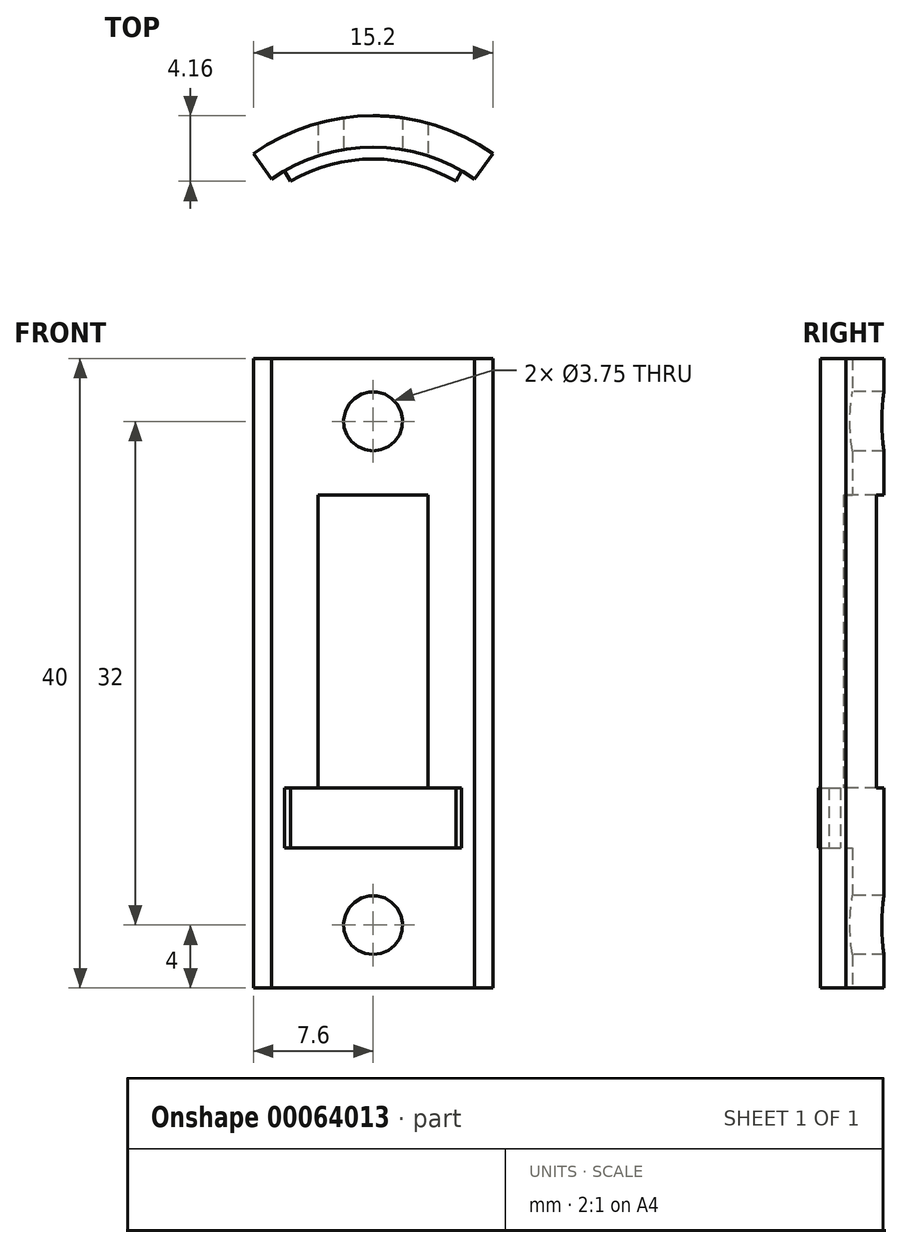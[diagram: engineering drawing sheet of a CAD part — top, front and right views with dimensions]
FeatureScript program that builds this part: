
annotation { "Feature Type Name" : "Feature", "Feature Type Description" : "" }
export const myFeature = defineFeature(function(context is Context, id is Id, definition is map)
    precondition{}
    {
        {
            var Q0;
            Q0=qCreatedBy(makeId("Top.planeOp"),FACE);
            var sketch = newSketch(context, id + "F0", { "sketchPlane" : qUnion([Q0])});
            skArc(sketch, "E0", {"start": v(6.45, 9.22) * mm, "mid": v(0, 11.25) * mm, "end": v(-6.45, 9.22) * mm});
            skArc(sketch, "E1", {"start": v(7.6, 10.85) * mm, "mid": v(0, 13.25) * mm, "end": v(-7.6, 10.85) * mm});
            skLineSegment(sketch, "E2", {"start": v(6.45, 9.22) * mm, "end": v(7.6, 10.85) * mm});
            skLineSegment(sketch, "E3", {"start": v(-6.45, 9.22) * mm, "end": v(-7.6, 10.85) * mm});
            skSolve(sketch);
        }
        {
            var Q0;
            Q0 = qSketchRegion(id + "F0", true);
            extrude(context, id + "F1", {"entities" : qUnion([Q0]), "depth" : 40 * mm});
        }
        {
            var Q0;
            Q0=qCreatedBy(makeId("Top.planeOp"),FACE);
            var sketch = newSketch(context, id + "F2", { "sketchPlane" : qUnion([Q0])});
            skArc(sketch, "E4", {"start": v(5.25, 9.1) * mm, "mid": v(0, 10.5) * mm, "end": v(-5.25, 9.1) * mm});
            skArc(sketch, "E5", {"start": v(5.62, 9.74) * mm, "mid": v(0, 11.25) * mm, "end": v(-5.62, 9.74) * mm});
            skLineSegment(sketch, "E6", {"start": v(-5.25, 9.1) * mm, "end": v(-5.62, 9.74) * mm});
            skLineSegment(sketch, "E7", {"start": v(5.25, 9.1) * mm, "end": v(5.62, 9.74) * mm});
            skSolve(sketch);
        }
        {
            var Q0;
            Q0 = qSketchRegion(id + "F2", true);
            extrude(context, id + "F3", {"entities" : qUnion([Q0]), "operationType" : NewBodyOperationType.ADD, "depth" : 12.7 * mm});
        }
        {
            var Q0;
            Q0 = qSketchRegion(id + "F2", true);
            extrude(context, id + "F4", {"entities" : qUnion([Q0]), "operationType" : NewBodyOperationType.REMOVE, "depth" : 8.9 * mm});
        }
        {
            var Q0;
            Q0=qCreatedBy(makeId("Front.planeOp"),FACE);
            var sketch = newSketch(context, id + "F5", { "sketchPlane" : qUnion([Q0])});
            skLineSegment(sketch, "E8", {"start": v(0, 36) * mm, "end": v(0, 4) * mm});
            skSolve(sketch);
        }
        {
            var Q0;
            Q0=sQuery(id+"F5.wireOp",VERTEX,"E8.start");
            var Q1;
            Q1=sQuery(id+"F5.wireOp",VERTEX,"E8.end");
            var Q2;
            Q2=makeQuery(id+"F1.opExtrude","SWEPT_BODY",BODY,{"disambiguationData":[OSD([sQuery(id+"F0.wireOp",EDGE,"E0"),sQuery(id+"F0.wireOp",EDGE,"E1"),sQuery(id+"F0.wireOp",EDGE,"E2"),sQuery(id+"F0.wireOp",EDGE,"E3")])]});
            hole(context, id + "F6", {"style" : HoleStyle.SIMPLE, "holeDiameter" : 3.75 * mm, "endStyle" : HoleEndStyle.THROUGH, "locations" : qUnion([Q0, Q1]), "scope" : qUnion([Q2])});
        }
        {
            var Q0;
            Q0=qCreatedBy(makeId("Front.planeOp"),FACE);
            var sketch = newSketch(context, id + "F7", { "sketchPlane" : qUnion([Q0])});
            skLineSegment(sketch, "E9.rect.bottom", {"start": v(-3.5, 12.7) * mm, "end": v(3.5, 12.7) * mm});
            skLineSegment(sketch, "E9.rect.top", {"start": v(3.5, 31.32) * mm, "end": v(-3.5, 31.32) * mm});
            skLineSegment(sketch, "E9.rect.left", {"start": v(-3.5, 12.7) * mm, "end": v(-3.5, 31.32) * mm});
            skLineSegment(sketch, "E9.rect.right", {"start": v(3.5, 12.7) * mm, "end": v(3.5, 31.32) * mm});
            skPoint(sketch, "E9.rect.middle", {"position": v(0, 22) * mm});
            skSolve(sketch);
        }
        {
            var Q0;
            Q0 = qSketchRegion(id + "F7", true);
            extrude(context, id + "F8", {"entities" : qUnion([Q0]), "operationType" : NewBodyOperationType.REMOVE, "oppositeDirection" : true, "depth" : 25.4 * mm});
        }
    });
